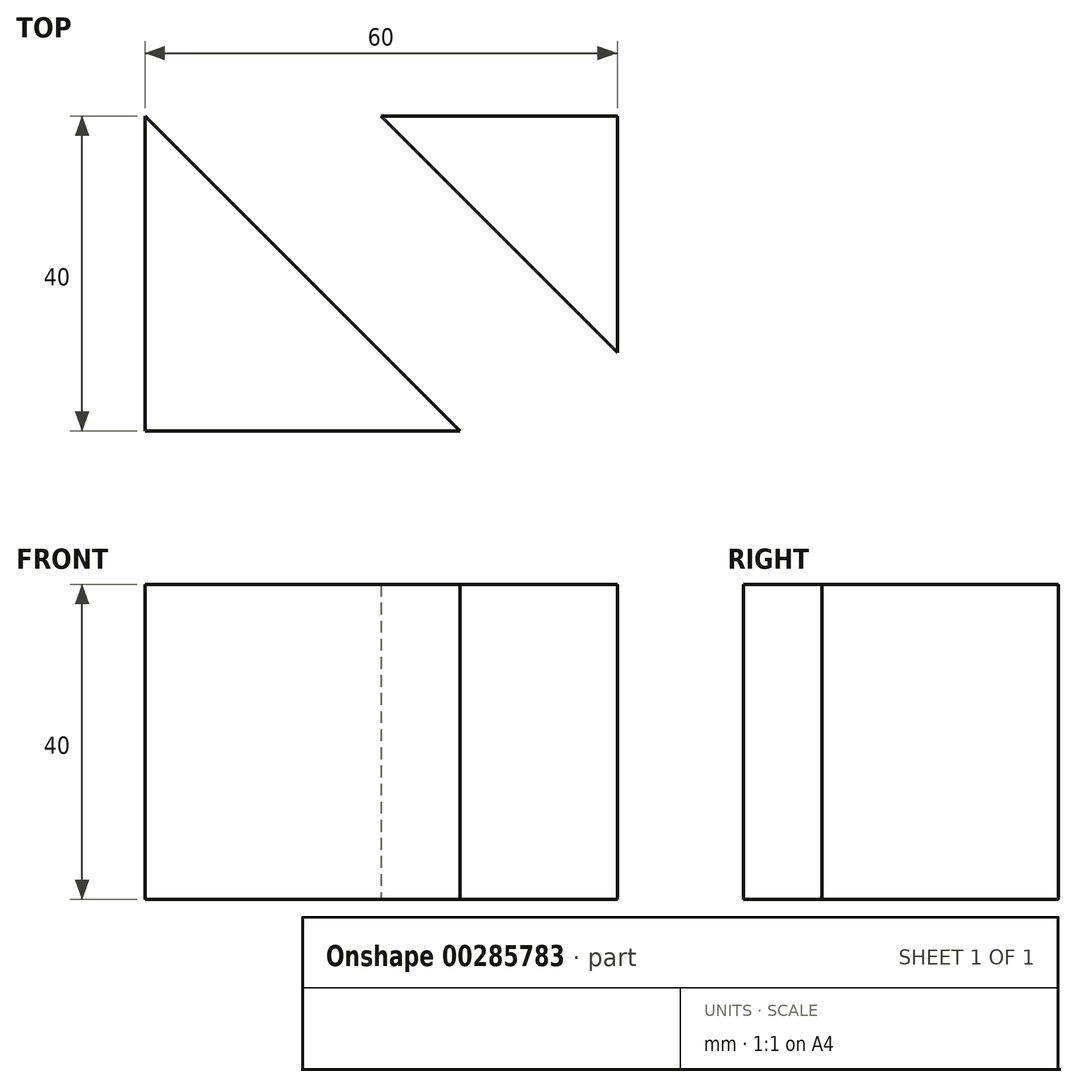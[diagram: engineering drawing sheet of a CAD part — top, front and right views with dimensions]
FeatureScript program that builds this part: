
annotation { "Feature Type Name" : "Feature", "Feature Type Description" : "" }
export const myFeature = defineFeature(function(context is Context, id is Id, definition is map)
    precondition{}
    {
        {
            var Q0;
            Q0=qCreatedBy(makeId("Top.planeOp"),FACE);
            var sketch = newSketch(context, id + "F0", { "sketchPlane" : qUnion([Q0])});
            skLineSegment(sketch, "E0.bottom", {"start": v(0, 0) * mm, "end": v(60, 0) * mm});
            skLineSegment(sketch, "E0.top", {"start": v(0, 40) * mm, "end": v(60, 40) * mm});
            skLineSegment(sketch, "E0.left", {"start": v(0, 0) * mm, "end": v(0, 40) * mm});
            skLineSegment(sketch, "E0.right", {"start": v(60, 0) * mm, "end": v(60, 40) * mm});
            skLineSegment(sketch, "E1", {"start": v(60, 0) * mm, "end": v(40, 0) * mm});
            skLineSegment(sketch, "E2", {"start": v(40, 0) * mm, "end": v(0, 40) * mm});
            skLineSegment(sketch, "E3", {"start": v(60, 0) * mm, "end": v(60, 10) * mm});
            skLineSegment(sketch, "E4", {"start": v(60, 40) * mm, "end": v(30, 40) * mm});
            skLineSegment(sketch, "E5", {"start": v(30, 40) * mm, "end": v(60, 10) * mm});
            skSolve(sketch);
        }
        {
            var Q0;
            Q0=makeQuery(id+"F0.imprint","IMPRINT",FACE,{"disambiguationData":[TD([[makeQuery(id+"F0.imprint","IMPRINT",EDGE,{"derivedFrom":sQuery(id+"F0.wireOp",EDGE,"E0.top")}),-1.0]])]});
            extrude(context, id + "F1", {"entities" : qUnion([Q0]), "depth" : 20 * mm});
        }
        {
            var Q0;
            Q0=makeQuery(id+"F0.imprint","IMPRINT",FACE,{"disambiguationData":[TD([[makeQuery(id+"F0.imprint","IMPRINT",EDGE,{"derivedFrom":sQuery(id+"F0.wireOp",EDGE,"E0.bottom")}),1.0]])]});
            var Q1;
            Q1=makeQuery(id+"F0.imprint","IMPRINT",FACE,{"disambiguationData":[TD([[makeQuery(id+"F0.imprint","IMPRINT",EDGE,{"derivedFrom":sQuery(id+"F0.wireOp",EDGE,"E0.right")}),1.0]])]});
            extrude(context, id + "F2", {"entities" : qUnion([Q0, Q1]), "operationType" : NewBodyOperationType.ADD, "depth" : 40 * mm});
        }
    });
